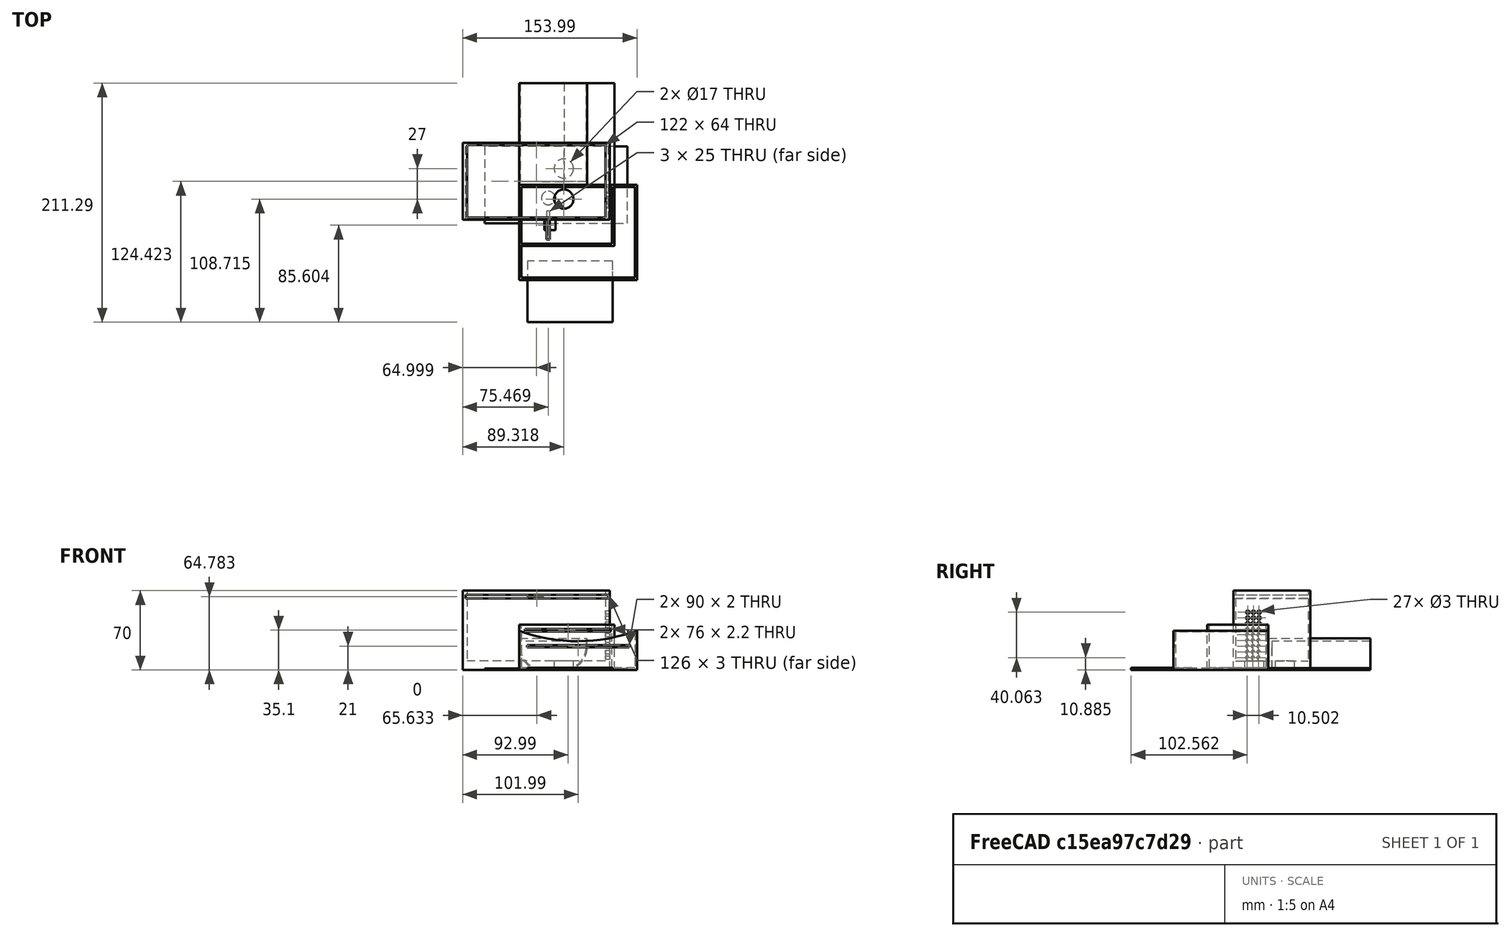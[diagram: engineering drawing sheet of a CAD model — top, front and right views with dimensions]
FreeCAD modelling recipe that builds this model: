
FCSTD DOCUMENT  (FreeCAD 1.2R20251230 (Git shallow))
Label: box_snic_esp32_1
License: Creative Commons Attribution 4.0
LicenseURL: https://creativecommons.org/licenses/by/4.0/
objects: Sketcher::SketchObject×18, PartDesign::Pocket×9, App::Point×8, PartDesign::Pad×8, PartDesign::Body×7, App::Link×2, App::FeaturePython×2, Assembly::JointGroup×1, Assembly::AssemblyObject×1, PartDesign::Fillet×1
note: 97 computed .brp shape members not serialized (recipe doc carries the construction recipe); baked Part::Feature solids carry a one-line shape summary decoded from their .brp

FEATURE [App::Point] Origin001  label="原点"
  Role = Origin
FEATURE [Sketcher::SketchObject] Sketch
  ArcFitTolerance = 1e-06
  AttachmentSupport = -> [Origin]
  ExternalTypes = [0]
  FullyConstrained = false
  MakeInternals = false
  MapMode = 5
  sketch-geometry (4):
    g0: LineSegment StartX=-49.9915 StartY=37.133 StartZ=0 EndX=-49.9915 EndY=-30.867 EndZ=0
    g1: LineSegment StartX=-49.9915 StartY=-30.867 StartZ=0 EndX=80.0085 EndY=-30.867 EndZ=0
    g2: LineSegment StartX=80.0085 StartY=-30.867 StartZ=0 EndX=80.0085 EndY=37.133 EndZ=0
    g3: LineSegment StartX=80.0085 StartY=37.133 StartZ=0 EndX=-49.9915 EndY=37.133 EndZ=0
  constraints (10):
    c: Coincident(g0,g1)
    c: Coincident(g1,g2)
    c: Coincident(g2,g3)
    c: Coincident(g3,g0)
    c: Vertical(g0)
    c: Vertical(g2)
    c: Horizontal(g1)
    c: Horizontal(g3)
    c: DistanceY(g2,g2) = 68
    c: DistanceX(g3,g3) = 130
FEATURE [PartDesign::Pad] Pad
  Direction = (0,0,1)
  Length = 70
  Length2 = 10
  Profile = -> Sketch
  ReferenceAxis = -> Sketch [N_Axis]
  Refine = true
  SideType = 0
  Suppressed = false
  Type = 0
  Type2 = 0
FEATURE [Sketcher::SketchObject] Sketch001
  ArcFitTolerance = 1e-06
  AttachmentSupport = -> [Pad]
  ExternalTypes = [0]
  FullyConstrained = false
  MakeInternals = false
  MapMode = 5
  Placement = pos=(0,0,70) rot=(0,0,1;0rad)
  sketch-geometry (4):
    g0: LineSegment StartX=-45.9915 StartY=35.133 StartZ=0 EndX=-45.9915 EndY=-28.867 EndZ=0
    g1: LineSegment StartX=-45.9915 StartY=-28.867 StartZ=0 EndX=76.0085 EndY=-28.867 EndZ=0
    g2: LineSegment StartX=76.0085 StartY=-28.867 StartZ=0 EndX=76.0085 EndY=35.133 EndZ=0
    g3: LineSegment StartX=76.0085 StartY=35.133 StartZ=0 EndX=-45.9915 EndY=35.133 EndZ=0
  constraints (10):
    c: Coincident(g0,g1)
    c: Coincident(g1,g2)
    c: Coincident(g2,g3)
    c: Coincident(g3,g0)
    c: Vertical(g0)
    c: Vertical(g2)
    c: Horizontal(g1)
    c: Horizontal(g3)
    c: DistanceX(g3,g3) = 122
    c: DistanceY(g0,g0) = 64
FEATURE [PartDesign::Pocket] Pocket
  BaseFeature = -> Pad
  Direction = (0,0,-1)
  Length = 62
  Length2 = 5
  Profile = -> Sketch001
  ReferenceAxis = -> Sketch001 [N_Axis]
  Refine = true
  SideType = 0
  Suppressed = false
  Type = 0
  Type2 = 0
FEATURE [Sketcher::SketchObject] Sketch002
  ArcFitTolerance = 1e-06
  AttachmentSupport = -> [Pocket]
  ExternalTypes = [0]
  FullyConstrained = false
  MakeInternals = false
  MapMode = 5
  Placement = pos=(0,-30.867,0) rot=(1,0,0;1.5708rad)
  sketch-geometry (4):
    g0: LineSegment StartX=-47.3565 StartY=66.2828 StartZ=0 EndX=-47.3565 EndY=63.2828 EndZ=0
    g1: LineSegment StartX=-47.3565 StartY=63.2828 StartZ=0 EndX=78.6435 EndY=63.2828 EndZ=0
    g2: LineSegment StartX=78.6435 StartY=63.2828 StartZ=0 EndX=78.6435 EndY=66.2828 EndZ=0
    g3: LineSegment StartX=78.6435 StartY=66.2828 StartZ=0 EndX=-47.3565 EndY=66.2828 EndZ=0
  constraints (10):
    c: Coincident(g0,g1)
    c: Coincident(g1,g2)
    c: Coincident(g2,g3)
    c: Coincident(g3,g0)
    c: Vertical(g0)
    c: Vertical(g2)
    c: Horizontal(g1)
    c: Horizontal(g3)
    c: Distance(g2,g2) = 3
    c: DistanceX(g3,g3) = 126
FEATURE [PartDesign::Pocket] Pocket001
  BaseFeature = -> Pocket
  Direction = (0,1,-2e-16)
  Length = 5
  Length2 = 5
  Profile = -> Sketch002
  ReferenceAxis = -> Sketch002 [N_Axis]
  Refine = true
  SideType = 0
  Suppressed = false
  Type = 1
  Type2 = 0
FEATURE [App::Point] Origin003  label="原点002"
  Role = Origin
FEATURE [Sketcher::SketchObject] Sketch003
  ArcFitTolerance = 1e-06
  AttachmentSupport = -> [Origin002]
  ExternalTypes = [0]
  FullyConstrained = false
  MakeInternals = false
  MapMode = 5
  sketch-geometry (4):
    g0: LineSegment StartX=-30.421 StartY=34 StartZ=0 EndX=-30.421 EndY=-34 EndZ=0
    g1: LineSegment StartX=-30.421 StartY=-34 StartZ=0 EndX=95.579 EndY=-34 EndZ=0
    g2: LineSegment StartX=95.579 StartY=-34 StartZ=0 EndX=95.579 EndY=34 EndZ=0
    g3: LineSegment StartX=95.579 StartY=34 StartZ=0 EndX=-30.421 EndY=34 EndZ=0
  constraints (10):
    c: Coincident(g0,g1)
    c: Coincident(g1,g2)
    c: Coincident(g2,g3)
    c: Coincident(g3,g0)
    c: Vertical(g2)
    c: Horizontal(g1)
    c: Horizontal(g3)
    c: DistanceX(g3,g3) = 126
    c: DistanceY(g2,g2) = 68
    c: Symmetric(g0,g0,g-1)
FEATURE [PartDesign::Pad] Pad001
  Direction = (0,0,1)
  Length = 1.2
  Length2 = 10
  Profile = -> Sketch003
  ReferenceAxis = -> Sketch003 [N_Axis]
  Refine = true
  SideType = 0
  Suppressed = false
  Type = 0
  Type2 = 0
FEATURE [PartDesign::Body] Body001  label="box_cover_1"
  AllowCompound = true
  Group = -> [Sketch003,Pad001]
  Origin = -> Origin002
  Tip = -> Pad001
FEATURE [Sketcher::SketchObject] Sketch004
  ArcFitTolerance = 1e-06
  AttachmentSupport = -> [Pocket001]
  ExternalTypes = [0]
  FullyConstrained = false
  MakeInternals = false
  MapMode = 5
  Placement = pos=(80.0085,0,0) rot=(0.57735,0.57735,0.57735;2.0944rad)
  sketch-geometry (27):
    g0: Circle CenterX=-18.6463 CenterY=35.9546 CenterZ=0 NormalX=0 NormalY=0 NormalZ=1 AngleXU=0 Radius=1.5
    g1: Circle CenterX=-13.6463 CenterY=35.9546 CenterZ=0 NormalX=0 NormalY=0 NormalZ=1 AngleXU=0 Radius=1.5
    g2: Circle CenterX=-8.64635 CenterY=35.9546 CenterZ=0 NormalX=0 NormalY=0 NormalZ=1 AngleXU=0 Radius=1.5
    g3: Circle CenterX=-18.6874 CenterY=30.9548 CenterZ=0 NormalX=0 NormalY=0 NormalZ=1 AngleXU=0 Radius=1.5
    g4: Circle CenterX=-13.6874 CenterY=30.9548 CenterZ=0 NormalX=0 NormalY=0 NormalZ=1 AngleXU=0 Radius=1.5
    g5: Circle CenterX=-8.68742 CenterY=30.9548 CenterZ=0 NormalX=0 NormalY=0 NormalZ=1 AngleXU=0 Radius=1.5
    g6: Circle CenterX=-18.7285 CenterY=25.9549 CenterZ=0 NormalX=0 NormalY=0 NormalZ=1 AngleXU=0 Radius=1.5
    g7: Circle CenterX=-13.7285 CenterY=25.9549 CenterZ=0 NormalX=0 NormalY=0 NormalZ=1 AngleXU=0 Radius=1.5
    g8: Circle CenterX=-8.72848 CenterY=25.9549 CenterZ=0 NormalX=0 NormalY=0 NormalZ=1 AngleXU=0 Radius=1.5
    g9: Circle CenterX=-18.6463 CenterY=20.885 CenterZ=0 NormalX=0 NormalY=0 NormalZ=1 AngleXU=0 Radius=1.5
    g10: Circle CenterX=-13.6463 CenterY=20.885 CenterZ=0 NormalX=0 NormalY=0 NormalZ=1 AngleXU=0 Radius=1.5
    g11: Circle CenterX=-8.64635 CenterY=20.885 CenterZ=0 NormalX=0 NormalY=0 NormalZ=1 AngleXU=0 Radius=1.5
    g12: Circle CenterX=-18.6874 CenterY=15.8852 CenterZ=0 NormalX=0 NormalY=0 NormalZ=1 AngleXU=0 Radius=1.5
    g13: Circle CenterX=-13.6874 CenterY=15.8852 CenterZ=0 NormalX=0 NormalY=0 NormalZ=1 AngleXU=0 Radius=1.5
    g14: Circle CenterX=-8.68742 CenterY=15.8852 CenterZ=0 NormalX=0 NormalY=0 NormalZ=1 AngleXU=0 Radius=1.5
    g15: Circle CenterX=-18.7285 CenterY=10.8854 CenterZ=0 NormalX=0 NormalY=0 NormalZ=1 AngleXU=0 Radius=1.5
    g16: Circle CenterX=-13.7285 CenterY=10.8854 CenterZ=0 NormalX=0 NormalY=0 NormalZ=1 AngleXU=0 Radius=1.5
    g17: Circle CenterX=-8.72848 CenterY=10.8854 CenterZ=0 NormalX=0 NormalY=0 NormalZ=1 AngleXU=0 Radius=1.5
    g18: Circle CenterX=-18.2265 CenterY=50.9487 CenterZ=0 NormalX=0 NormalY=0 NormalZ=1 AngleXU=0 Radius=1.5
    g19: Circle CenterX=-13.2265 CenterY=50.9487 CenterZ=0 NormalX=0 NormalY=0 NormalZ=1 AngleXU=0 Radius=1.5
    g20: Circle CenterX=-8.22651 CenterY=50.9487 CenterZ=0 NormalX=0 NormalY=0 NormalZ=1 AngleXU=0 Radius=1.5
    g21: Circle CenterX=-18.2676 CenterY=45.9489 CenterZ=0 NormalX=0 NormalY=0 NormalZ=1 AngleXU=0 Radius=1.5
    g22: Circle CenterX=-13.2676 CenterY=45.9489 CenterZ=0 NormalX=0 NormalY=0 NormalZ=1 AngleXU=0 Radius=1.5
    g23: Circle CenterX=-8.26758 CenterY=45.9489 CenterZ=0 NormalX=0 NormalY=0 NormalZ=1 AngleXU=0 Radius=1.5
    g24: Circle CenterX=-18.3086 CenterY=40.9491 CenterZ=0 NormalX=0 NormalY=0 NormalZ=1 AngleXU=0 Radius=1.5
    g25: Circle CenterX=-13.3086 CenterY=40.9491 CenterZ=0 NormalX=0 NormalY=0 NormalZ=1 AngleXU=0 Radius=1.5
    g26: Circle CenterX=-8.30865 CenterY=40.9491 CenterZ=0 NormalX=0 NormalY=0 NormalZ=1 AngleXU=0 Radius=1.5
  constraints (27):
    c: Diameter(g0) = 3
    c: Diameter(g1) = 3
    c: Diameter(g2) = 3
    c: Diameter(g3) = 3
    c: Diameter(g6) = 3
    c: Diameter(g9) = 3
    c: Diameter(g12) = 3
    c: Diameter(g15) = 3
    c: Diameter(g4) = 3
    c: Diameter(g7) = 3
    c: Diameter(g10) = 3
    c: Diameter(g13) = 3
    c: Diameter(g16) = 3
    c: Diameter(g5) = 3
    c: Diameter(g8) = 3
    c: Diameter(g11) = 3
    c: Diameter(g14) = 3
    c: Diameter(g17) = 3
    c: Diameter(g18) = 3
    c: Diameter(g19) = 3
    c: Diameter(g20) = 3
    c: Diameter(g21) = 3
    c: Diameter(g24) = 3
    c: Diameter(g22) = 3
    c: Diameter(g25) = 3
    c: Diameter(g23) = 3
    c: Diameter(g26) = 3
FEATURE [PartDesign::Pocket] Pocket002
  BaseFeature = -> Pocket001
  Direction = (-1,0,0)
  Length = 5
  Length2 = 5
  Profile = -> Sketch004
  ReferenceAxis = -> Sketch004 [N_Axis]
  Refine = true
  SideType = 0
  Suppressed = false
  Type = 0
  Type2 = 0
FEATURE [App::Point] Origin005  label="原点004"
  Role = Origin
FEATURE [App::Link] Body002
  LinkedObject = -> Body
FEATURE [App::FeaturePython] GroundedJoint  # Assembly grounded joint (typed FeaturePython)
  ObjectToGround = -> Body002
FEATURE [App::Link] Body003
  LinkPlacement = pos=(-16.8507,1.18925,56.2573) rot=(0,0,1;0rad)
  LinkedObject = -> Body001
  Placement = pos=(-16.8507,1.18925,56.2573) rot=(0,0,1;0rad)
FEATURE [App::FeaturePython] Joint  label="Parallel"  # Assembly joint (typed FeaturePython)
  Angle = 0
  AngleMax = 0
  AngleMin = 0
  Detach1 = false
  Detach2 = false
  Distance = 0
  Distance2 = 0
  EnableAngleMax = false
  EnableAngleMin = false
  EnableLengthMax = false
  EnableLengthMin = false
  JointType = 6 (Parallel)
  LengthMax = 0
  LengthMin = 0
  Suppressed = false
FEATURE [Assembly::JointGroup] Joints
  Group = -> [GroundedJoint,Joint]
FEATURE [Assembly::AssemblyObject] Assembly  label="box_assembly_1"
  Group = -> [Joints,Body002,GroundedJoint,Body003,Joint]
  Origin = -> Origin004
  Type = Assembly
FEATURE [Sketcher::SketchObject] Sketch005
  ArcFitTolerance = 1e-06
  AttachmentSupport = -> [Pocket002]
  ExternalTypes = [0]
  FullyConstrained = false
  MakeInternals = false
  MapMode = 5
  Placement = pos=(0,0,0) rot=(1,0,0;3.14159rad)
  sketch-geometry (2):
    g0: Circle CenterX=39.3276 CenterY=12.575 CenterZ=0 NormalX=0 NormalY=0 NormalZ=1 AngleXU=0 Radius=8.5
    g1: Circle CenterX=39.3276 CenterY=-14.425 CenterZ=0 NormalX=0 NormalY=0 NormalZ=1 AngleXU=0 Radius=8.5
  constraints (3):
    c: Diameter(g0) = 17
    c: Diameter(g1) = 17
    c: Distance(g0,g1) = 10
FEATURE [PartDesign::Pocket] Pocket003
  BaseFeature = -> Pocket002
  Direction = (0,0,1)
  Length = 5
  Length2 = 5
  Profile = -> Sketch005
  ReferenceAxis = -> Sketch005 [N_Axis]
  Refine = true
  SideType = 0
  Suppressed = false
  Type = 1
  Type2 = 0
FEATURE [PartDesign::Body] Body  label="box_1"
  AllowCompound = true
  Group = -> [Sketch,Pad,Sketch001,Pocket,Sketch002,Pocket001,Sketch004,Pocket002,Sketch005,Pocket003]
  Origin = -> Origin
  Tip = -> Pocket003
FEATURE [App::Point] Origin007  label="原点006"
  Role = Origin
FEATURE [Sketcher::SketchObject] Sketch006
  ArcFitTolerance = 1e-06
  AttachmentSupport = -> [Origin006]
  ExternalTypes = [0]
  FullyConstrained = false
  MakeInternals = false
  MapMode = 5
  sketch-geometry (8):
    g0: LineSegment StartX=0 StartY=0 StartZ=0 EndX=0 EndY=-84 EndZ=0
    g1: LineSegment StartX=0 StartY=-84 StartZ=0 EndX=104 EndY=-84 EndZ=0
    g2: LineSegment StartX=104 StartY=-84 StartZ=0 EndX=104 EndY=0 EndZ=0
    g3: LineSegment StartX=104 StartY=0 StartZ=0 EndX=0 EndY=0 EndZ=0
    g4: LineSegment StartX=22.0642 StartY=-30 StartZ=0 EndX=22.0642 EndY=-40 EndZ=0
    g5: LineSegment StartX=22.0642 StartY=-40 StartZ=0 EndX=32.0642 EndY=-40 EndZ=0
    g6: LineSegment StartX=32.0642 StartY=-40 StartZ=0 EndX=32.0642 EndY=-30 EndZ=0
    g7: LineSegment StartX=32.0642 StartY=-30 StartZ=0 EndX=22.0642 EndY=-30 EndZ=0
  constraints (22):
    c: Coincident(g0,g1)
    c: Coincident(g1,g2)
    c: Coincident(g2,g3)
    c: Coincident(g3,g0)
    c: Vertical(g0)
    c: Vertical(g2)
    c: Horizontal(g1)
    c: Horizontal(g3)
    c: Coincident(g0,g-1)
    c: DistanceX(g1,g1) = 104
    c: DistanceY(g0,g0) = 84
    c: Coincident(g4,g5)
    c: Coincident(g5,g6)
    c: Coincident(g6,g7)
    c: Coincident(g7,g4)
    c: Vertical(g4)
    c: Vertical(g6)
    c: Horizontal(g5)
    c: Horizontal(g7)
    c: Distance(g7,g7) = 10
    c: Distance(g6,g6) = 10
    c: Distance(g3,g7) = 30
FEATURE [PartDesign::Pad] Pad002
  Direction = (0,0,1)
  Length = 36
  Length2 = 10
  Profile = -> Sketch006
  ReferenceAxis = -> Sketch006 [N_Axis]
  Refine = true
  SideType = 0
  Suppressed = false
  Type = 0
  Type2 = 0
FEATURE [Sketcher::SketchObject] Sketch007
  ArcFitTolerance = 1e-06
  AttachmentSupport = -> [Pad002]
  ExternalTypes = [0]
  FullyConstrained = true
  MakeInternals = false
  MapMode = 5
  Placement = pos=(0,0,36) rot=(0,0,1;0rad)
  sketch-geometry (4):
    g0: LineSegment StartX=2 StartY=-2 StartZ=0 EndX=2 EndY=-82 EndZ=0
    g1: LineSegment StartX=2 StartY=-82 StartZ=0 EndX=102 EndY=-82 EndZ=0
    g2: LineSegment StartX=102 StartY=-82 StartZ=0 EndX=102 EndY=-2 EndZ=0
    g3: LineSegment StartX=102 StartY=-2 StartZ=0 EndX=2 EndY=-2 EndZ=0
  constraints (12):
    c: Coincident(g0,g1)
    c: Coincident(g1,g2)
    c: Coincident(g2,g3)
    c: Coincident(g3,g0)
    c: Vertical(g0)
    c: Vertical(g2)
    c: Horizontal(g1)
    c: Horizontal(g3)
    c: DistanceX(g1,g1) = 100
    c: DistanceY(g2,g2) = 80
    c: Distance(g-1,g3) = 2
    c: Distance(g-2,g0) = 2
FEATURE [PartDesign::Pocket] Pocket004
  BaseFeature = -> Pad002
  Direction = (0,0,-1)
  Length = 34
  Length2 = 5
  Profile = -> Sketch007
  ReferenceAxis = -> Sketch007 [N_Axis]
  Refine = true
  SideType = 0
  Suppressed = false
  Type = 0
  Type2 = 0
FEATURE [Sketcher::SketchObject] Sketch008
  ArcFitTolerance = 1e-06
  AttachmentSupport = -> [Pocket004]
  ExternalTypes = [0]
  FullyConstrained = false
  MakeInternals = false
  MapMode = 5
  Placement = pos=(0,-84,0) rot=(1,0,0;1.5708rad)
  sketch-geometry (4):
    g0: ArcOfCircle CenterX=51.7505 CenterY=177.652 CenterZ=0 NormalX=0 NormalY=0 NormalZ=1 AngleXU=0 Radius=152.263 StartAngle=4.34938 EndAngle=5.07539
    g1: LineSegment StartX=-2.31593 StartY=35.3107 StartZ=0 EndX=-2.31593 EndY=49.5769 EndZ=0
    g2: LineSegment StartX=-2.31593 StartY=49.5769 StartZ=0 EndX=106.776 EndY=49.5769 EndZ=0
    g3: LineSegment StartX=105.817 StartY=35.3107 StartZ=0 EndX=106.776 EndY=49.5769 EndZ=0
  constraints (6):
    c: Coincident(g1,g0)
    c: Vertical(g1)
    c: Coincident(g2,g1)
    c: Horizontal(g2)
    c: Coincident(g3,g0)
    c: Coincident(g3,g2)
FEATURE [PartDesign::Pocket] Pocket005
  BaseFeature = -> Pocket004
  Direction = (0,1,-2e-16)
  Length = 5
  Length2 = 5
  Profile = -> Sketch008
  ReferenceAxis = -> Sketch008 [N_Axis]
  Refine = true
  SideType = 0
  Suppressed = false
  Type = 1
  Type2 = 0
FEATURE [Sketcher::SketchObject] Sketch009
  ArcFitTolerance = 1e-06
  AttachmentSupport = -> [Pocket005]
  ExternalTypes = [0]
  FullyConstrained = true
  MakeInternals = false
  MapMode = 5
  Placement = pos=(0,0,0) rot=(0,0.707107,0.707107;3.14159rad)
  sketch-geometry (4):
    g0: LineSegment StartX=-97 StartY=22 StartZ=0 EndX=-97 EndY=20 EndZ=0
    g1: LineSegment StartX=-97 StartY=20 StartZ=0 EndX=-7 EndY=20 EndZ=0
    g2: LineSegment StartX=-7 StartY=20 StartZ=0 EndX=-7 EndY=22 EndZ=0
    g3: LineSegment StartX=-7 StartY=22 StartZ=0 EndX=-97 EndY=22 EndZ=0
  constraints (12):
    c: Coincident(g0,g1)
    c: Coincident(g1,g2)
    c: Coincident(g2,g3)
    c: Coincident(g3,g0)
    c: Vertical(g0)
    c: Vertical(g2)
    c: Horizontal(g1)
    c: Horizontal(g3)
    c: DistanceY(g2,g2) = 2
    c: DistanceX(g1,g1) = 90
    c: Distance(g-1,g1) = 20
    c: Distance(g-2,g2) = 7
FEATURE [PartDesign::Pocket] Pocket006
  BaseFeature = -> Pocket005
  Direction = (0,-1,2e-16)
  Length = 5
  Length2 = 5
  Profile = -> Sketch009
  ReferenceAxis = -> Sketch009 [N_Axis]
  Refine = true
  SideType = 0
  Suppressed = false
  Type = 1
  Type2 = 0
FEATURE [PartDesign::Body] Body004  label="box_2"
  AllowCompound = true
  Group = -> [Sketch006,Pad002,Sketch007,Pocket004,Sketch008,Pocket005,Sketch009,Pocket006]
  Origin = -> Origin006
  Tip = -> Pocket006
FEATURE [App::Point] Origin009  label="原点008"
  Role = Origin
FEATURE [Sketcher::SketchObject] Sketch010
  ArcFitTolerance = 1e-06
  AttachmentSupport = -> [Origin008]
  ExternalTypes = [0]
  FullyConstrained = true
  MakeInternals = false
  MapMode = 5
  sketch-geometry (4):
    g0: LineSegment StartX=0 StartY=0 StartZ=0 EndX=84 EndY=0 EndZ=0
    g1: LineSegment StartX=84 StartY=0 StartZ=0 EndX=84 EndY=90 EndZ=0
    g2: LineSegment StartX=84 StartY=90 StartZ=0 EndX=0 EndY=90 EndZ=0
    g3: LineSegment StartX=0 StartY=90 StartZ=0 EndX=0 EndY=0 EndZ=0
  constraints (11):
    c: Coincident(g0,g1)
    c: Coincident(g1,g2)
    c: Coincident(g2,g3)
    c: Coincident(g3,g0)
    c: Horizontal(g0)
    c: Horizontal(g2)
    c: Vertical(g1)
    c: Vertical(g3)
    c: Coincident(g0,g-1)
    c: DistanceY(g1,g1) = 90
    c: DistanceX(g2,g2) = 84
FEATURE [PartDesign::Pad] Pad003
  Direction = (0,0,1)
  Length = 1.6
  Length2 = 10
  Profile = -> Sketch010
  ReferenceAxis = -> Sketch010 [N_Axis]
  Refine = true
  SideType = 0
  Suppressed = false
  Type = 0
  Type2 = 0
FEATURE [PartDesign::Body] Body005  label="box_cover_2"
  AllowCompound = true
  Group = -> [Sketch010,Pad003]
  Origin = -> Origin008
  Tip = -> Pad003
FEATURE [App::Point] Origin011  label="原点010"
  Role = Origin
FEATURE [Sketcher::SketchObject] Sketch011
  ArcFitTolerance = 1e-06
  AttachmentSupport = -> [Origin010]
  ExternalTypes = [0]
  FullyConstrained = false
  MakeInternals = false
  MapMode = 5
  sketch-geometry (9):
    g0: LineSegment StartX=0 StartY=0 StartZ=0 EndX=0 EndY=-54 EndZ=0
    g1: LineSegment StartX=0 StartY=-54 StartZ=0 EndX=84 EndY=-54 EndZ=0
    g2: LineSegment StartX=84 StartY=-54 StartZ=0 EndX=84 EndY=0 EndZ=0
    g3: LineSegment StartX=84 StartY=0 StartZ=0 EndX=0 EndY=0 EndZ=0
    g4: Circle CenterX=25.609 CenterY=-11.6323 CenterZ=0 NormalX=0 NormalY=0 NormalZ=1 AngleXU=0 Radius=6
    g5: LineSegment StartX=23.9791 StartY=-23.1864 StartZ=0 EndX=23.9791 EndY=-48.1864 EndZ=0
    g6: LineSegment StartX=23.9791 StartY=-48.1864 StartZ=0 EndX=26.9791 EndY=-48.1864 EndZ=0
    g7: LineSegment StartX=26.9791 StartY=-48.1864 StartZ=0 EndX=26.9791 EndY=-23.1864 EndZ=0
    g8: LineSegment StartX=26.9791 StartY=-23.1864 StartZ=0 EndX=23.9791 EndY=-23.1864 EndZ=0
  constraints (22):
    c: Coincident(g0,g1)
    c: Coincident(g1,g2)
    c: Coincident(g2,g3)
    c: Coincident(g3,g0)
    c: Vertical(g0)
    c: Vertical(g2)
    c: Horizontal(g1)
    c: Horizontal(g3)
    c: Coincident(g0,g-1)
    c: DistanceX(g3,g3) = 84
    c: DistanceY(g2,g2) = 54
    c: Diameter(g4) = 12
    c: Coincident(g5,g6)
    c: Coincident(g6,g7)
    c: Coincident(g7,g8)
    c: Coincident(g8,g5)
    c: Vertical(g5)
    c: Vertical(g7)
    c: Horizontal(g6)
    c: Horizontal(g8)
    c: DistanceY(g7,g7) = 25
    c: DistanceX(g8,g8) = 3
FEATURE [PartDesign::Pad] Pad004
  Direction = (0,0,1)
  Length = 2
  Length2 = 10
  Profile = -> Sketch011
  ReferenceAxis = -> Sketch011 [N_Axis]
  Refine = true
  SideType = 0
  Suppressed = false
  Type = 0
  Type2 = 0
FEATURE [Sketcher::SketchObject] Sketch012
  ArcFitTolerance = 1e-06
  AttachmentSupport = -> [Pad004]
  ExternalTypes = [0]
  FullyConstrained = true
  MakeInternals = false
  MapMode = 5
  Placement = pos=(0,0,2) rot=(0,0,1;0rad)
  sketch-geometry (8):
    g0: LineSegment StartX=0 StartY=0 StartZ=0 EndX=0 EndY=-54 EndZ=0
    g1: LineSegment StartX=0 StartY=-54 StartZ=0 EndX=84 EndY=-54 EndZ=0
    g2: LineSegment StartX=84 StartY=-54 StartZ=0 EndX=84 EndY=0 EndZ=0
    g3: LineSegment StartX=84 StartY=0 StartZ=0 EndX=0 EndY=0 EndZ=0
    g4: LineSegment StartX=2 StartY=-2 StartZ=0 EndX=2 EndY=-52 EndZ=0
    g5: LineSegment StartX=2 StartY=-52 StartZ=0 EndX=82 EndY=-52 EndZ=0
    g6: LineSegment StartX=82 StartY=-52 StartZ=0 EndX=82 EndY=-2 EndZ=0
    g7: LineSegment StartX=82 StartY=-2 StartZ=0 EndX=2 EndY=-2 EndZ=0
  constraints (23):
    c: Coincident(g0,g1)
    c: Coincident(g1,g2)
    c: Coincident(g2,g3)
    c: Coincident(g3,g0)
    c: Vertical(g0)
    c: Vertical(g2)
    c: Horizontal(g1)
    c: Horizontal(g3)
    c: Coincident(g0,g-1)
    c: DistanceX(g1,g1) = 84
    c: DistanceY(g2,g2) = 54
    c: Coincident(g4,g5)
    c: Coincident(g5,g6)
    c: Coincident(g6,g7)
    c: Coincident(g7,g4)
    c: Vertical(g4)
    c: Vertical(g6)
    c: Horizontal(g5)
    c: Horizontal(g7)
    c: DistanceY(g6,g6) = 50
    c: DistanceX(g7,g7) = 80
    c: Distance(g1,g5) = 2
    c: Distance(g0,g4) = 2
FEATURE [PartDesign::Pad] Pad005
  BaseFeature = -> Pad004
  Direction = (0,0,1)
  Length = 38
  Length2 = 10
  Profile = -> Sketch012
  ReferenceAxis = -> Sketch012 [N_Axis]
  Refine = true
  SideType = 0
  Suppressed = false
  Type = 0
  Type2 = 0
FEATURE [Sketcher::SketchObject] Sketch013
  ArcFitTolerance = 1e-06
  AttachmentSupport = -> [Pad005]
  ExternalTypes = [0]
  FullyConstrained = true
  MakeInternals = false
  MapMode = 5
  Placement = pos=(0,0,0) rot=(0,0.707107,0.707107;3.14159rad)
  sketch-geometry (4):
    g0: LineSegment StartX=-81 StartY=36.2 StartZ=0 EndX=-81 EndY=34 EndZ=0
    g1: LineSegment StartX=-81 StartY=34 StartZ=0 EndX=-5 EndY=34 EndZ=0
    g2: LineSegment StartX=-5 StartY=34 StartZ=0 EndX=-5 EndY=36.2 EndZ=0
    g3: LineSegment StartX=-5 StartY=36.2 StartZ=0 EndX=-81 EndY=36.2 EndZ=0
  constraints (12):
    c: Coincident(g0,g1)
    c: Coincident(g1,g2)
    c: Coincident(g2,g3)
    c: Coincident(g3,g0)
    c: Vertical(g0)
    c: Vertical(g2)
    c: Horizontal(g1)
    c: Horizontal(g3)
    c: DistanceY(g0,g0) = 2.2
    c: DistanceX(g3,g3) = 76
    c: Distance(g-2,g2) = 5
    c: Distance(g-1,g1) = 34
FEATURE [PartDesign::Pocket] Pocket007
  BaseFeature = -> Pad005
  Direction = (0,-1,2e-16)
  Length = 5
  Length2 = 5
  Profile = -> Sketch013
  ReferenceAxis = -> Sketch013 [N_Axis]
  Refine = true
  SideType = 0
  Suppressed = false
  Type = 1
  Type2 = 0
FEATURE [PartDesign::Body] Body006  label="box_3"
  AllowCompound = true
  Group = -> [Sketch011,Pad004,Sketch012,Pad005,Sketch013,Pocket007]
  Origin = -> Origin010
  Tip = -> Pocket007
FEATURE [App::Point] Origin013  label="原点012"
  Role = Origin
FEATURE [Sketcher::SketchObject] Sketch014
  ArcFitTolerance = 1e-06
  AttachmentSupport = -> [Origin012]
  ExternalTypes = [0]
  FullyConstrained = false
  MakeInternals = false
  MapMode = 5
  sketch-geometry (4):
    g0: LineSegment StartX=7.33056 StartY=-67.2875 StartZ=0 EndX=7.33056 EndY=-121.288 EndZ=0
    g1: LineSegment StartX=7.33056 StartY=-121.288 StartZ=0 EndX=82.3306 EndY=-121.288 EndZ=0
    g2: LineSegment StartX=82.3306 StartY=-121.288 StartZ=0 EndX=82.3306 EndY=-67.2875 EndZ=0
    g3: LineSegment StartX=82.3306 StartY=-67.2875 StartZ=0 EndX=7.33056 EndY=-67.2875 EndZ=0
  constraints (10):
    c: Coincident(g0,g1)
    c: Coincident(g1,g2)
    c: Coincident(g2,g3)
    c: Coincident(g3,g0)
    c: Vertical(g0)
    c: Vertical(g2)
    c: Horizontal(g1)
    c: Horizontal(g3)
    c: DistanceX(g1,g1) = 75
    c: DistanceY(g2,g2) = 54
FEATURE [PartDesign::Pad] Pad006
  Direction = (0,0,1)
  Length = 1.8
  Length2 = 10
  Profile = -> Sketch014
  ReferenceAxis = -> Sketch014 [N_Axis]
  Refine = true
  SideType = 0
  Suppressed = false
  Type = 0
  Type2 = 0
FEATURE [PartDesign::Body] Body007  label="box_cover_3"
  AllowCompound = true
  Group = -> [Sketch014,Pad006]
  Origin = -> Origin012
  Tip = -> Pad006
FEATURE [App::Point] Origin015  label="原点014"
  Role = Origin
FEATURE [Sketcher::SketchObject] Sketch015
  ArcFitTolerance = 1e-06
  AttachmentSupport = -> [Origin014]
  ExternalTypes = [0]
  FullyConstrained = true
  MakeInternals = false
  MapMode = 5
  sketch-geometry (4):
    g0: LineSegment StartX=0 StartY=0 StartZ=0 EndX=60 EndY=0 EndZ=0
    g1: LineSegment StartX=60 StartY=0 StartZ=0 EndX=60 EndY=90 EndZ=0
    g2: LineSegment StartX=60 StartY=90 StartZ=0 EndX=0 EndY=90 EndZ=0
    g3: LineSegment StartX=0 StartY=90 StartZ=0 EndX=0 EndY=0 EndZ=0
  constraints (11):
    c: Coincident(g0,g1)
    c: Coincident(g1,g2)
    c: Coincident(g2,g3)
    c: Coincident(g3,g0)
    c: Horizontal(g0)
    c: Horizontal(g2)
    c: Vertical(g1)
    c: Vertical(g3)
    c: Coincident(g0,g-1)
    c: DistanceY(g1,g1) = 90
    c: DistanceX(g2,g2) = 60
FEATURE [PartDesign::Pad] Pad007
  Direction = (0,0,1)
  Length = 28
  Length2 = 10
  Profile = -> Sketch015
  ReferenceAxis = -> Sketch015 [N_Axis]
  Refine = true
  SideType = 0
  Suppressed = false
  Type = 0
  Type2 = 0
FEATURE [Sketcher::SketchObject] Sketch016
  ArcFitTolerance = 1e-06
  AttachmentSupport = -> [Pad007]
  ExternalTypes = [0]
  FullyConstrained = true
  MakeInternals = false
  MapMode = 5
  Placement = pos=(0,90,0) rot=(0,0.707107,0.707107;3.14159rad)
FEATURE [PartDesign::Fillet] Fillet
  Base = -> Pad007 [Edge11,Edge6]
  BaseFeature = -> Pad007
  Radius = 20
  Refine = true
  SupportTransform = false
  Suppressed = false
  UseAllEdges = false
FEATURE [Sketcher::SketchObject] Sketch017
  ArcFitTolerance = 1e-06
  AttachmentSupport = -> [Fillet]
  ExternalTypes = [0,0,0,0,0,0]
  FullyConstrained = false
  MakeInternals = false
  MapMode = 5
  Placement = pos=(0,90,0) rot=(0,0.707107,0.707107;3.14159rad)
  sketch-geometry (7):
    g0: LineSegment StartX=-58.9982 StartY=25.2178 StartZ=0 EndX=-1.00896 EndY=25.2178 EndZ=0
    g1: LineSegment StartX=-1.00896 StartY=25.2178 StartZ=0 EndX=-1.00896 EndY=19.8108 EndZ=0
    g2: LineSegment StartX=-58.9982 StartY=25.2178 StartZ=0 EndX=-58.9982 EndY=19.9184 EndZ=0
    g3: LineSegment StartX=-39.7511 StartY=1.00322 StartZ=0 EndX=-39.5612 EndY=1.00802 EndZ=0
    g4: ArcOfCircle CenterX=-20 CenterY=20 CenterZ=0 NormalX=0 NormalY=0 NormalZ=1 AngleXU=0 Radius=18.992 StartAngle=4.71239 EndAngle=6.27322
    g5: ArcOfCircle CenterX=-40 CenterY=20 CenterZ=0 NormalX=0 NormalY=0 NormalZ=1 AngleXU=0 Radius=18.9984 StartAngle=3.14589 EndAngle=4.72549
    g6: LineSegment StartX=-20 StartY=1.00802 StartZ=0 EndX=-39.5612 EndY=1.00802 EndZ=0
  constraints (11):
    c: Horizontal(g0)
    c: Coincident(g1,g0)
    c: Vertical(g1)
    c: Coincident(g2,g0)
    c: Vertical(g2)
    c: Coincident(g4,g1)
    c: Coincident(g5,g2)
    c: Coincident(g5,g3)
    c: Coincident(g6,g4)
    c: Coincident(g6,g3)
    c: Horizontal(g6)
FEATURE [PartDesign::Pocket] Pocket008
  BaseFeature = -> Fillet
  Direction = (0,-1,2e-16)
  Length = 87
  Length2 = 5
  Profile = -> Sketch017
  ReferenceAxis = -> Sketch017 [N_Axis]
  Refine = true
  SideType = 0
  Suppressed = false
  Type = 0
  Type2 = 0
FEATURE [PartDesign::Body] Body008  label="box_inner_4"
  AllowCompound = true
  Group = -> [Sketch015,Pad007,Sketch016,Fillet,Sketch017,Pocket008]
  Origin = -> Origin014
  Tip = -> Pocket008
